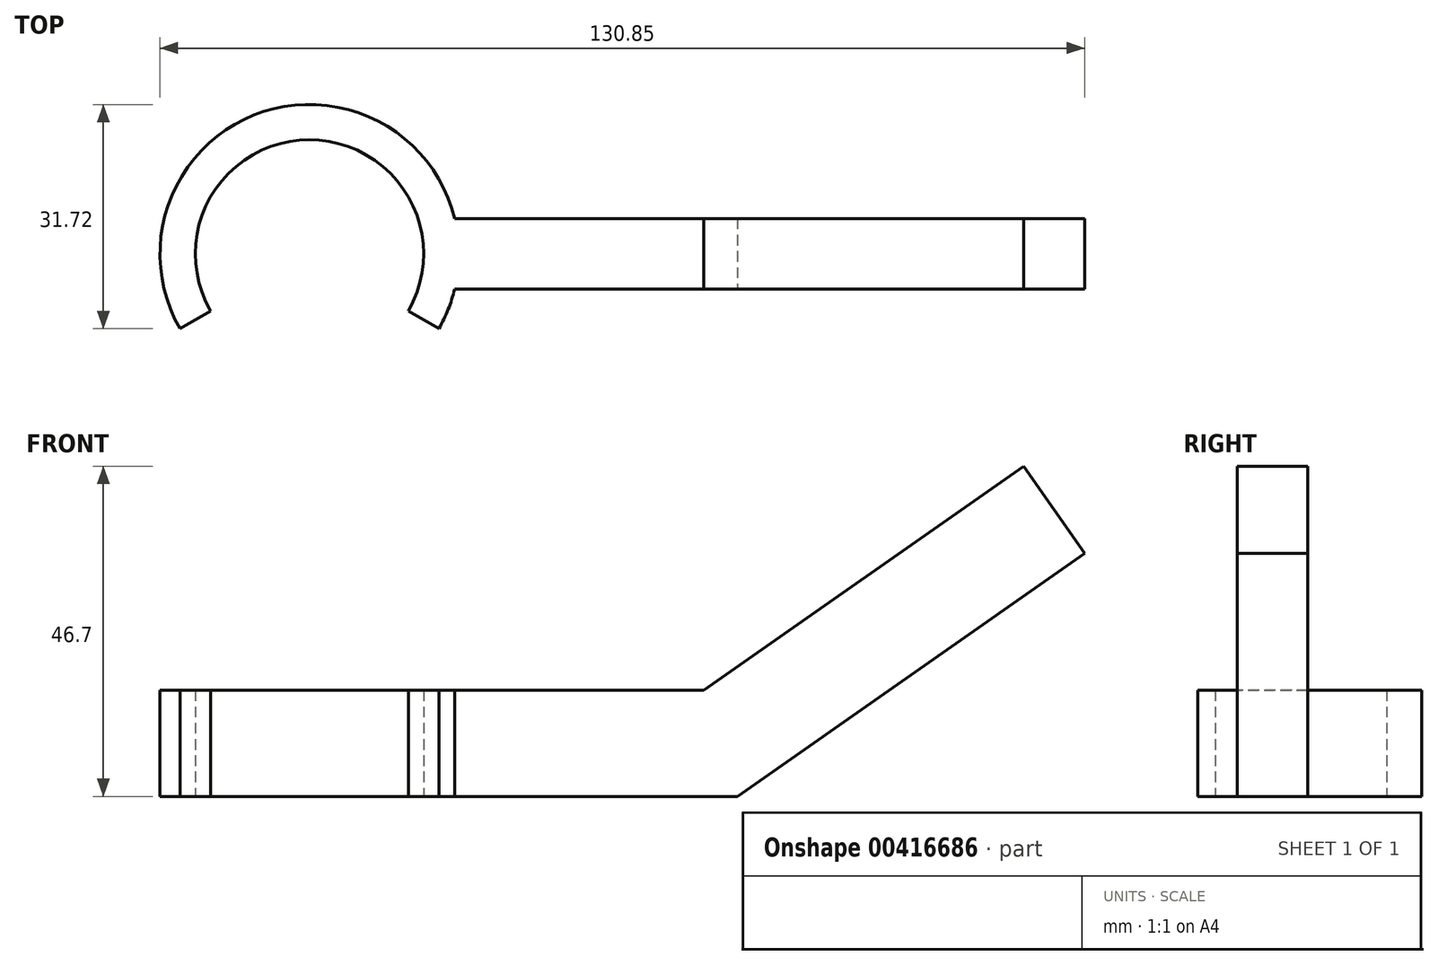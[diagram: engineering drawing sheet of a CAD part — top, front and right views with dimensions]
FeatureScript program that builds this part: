
annotation { "Feature Type Name" : "Feature", "Feature Type Description" : "" }
export const myFeature = defineFeature(function(context is Context, id is Id, definition is map)
    precondition{}
    {
        {
            var Q0;
            Q0=qCreatedBy(makeId("Top.planeOp"),FACE);
            var sketch = newSketch(context, id + "F0", { "sketchPlane" : qUnion([Q0])});
            skLineSegment(sketch, "E0", {"start": v(0, 0) * mm, "end": v(-24.9, -14.37) * mm, "construction": true});
            skLineSegment(sketch, "E1", {"start": v(0, 0) * mm, "end": v(22.76, -13.14) * mm, "construction": true});
            skPoint(sketch, "E2", {"position": v(-13.99, -8.08) * mm});
            skPoint(sketch, "E3", {"position": v(13.99, -8.07) * mm});
            skPoint(sketch, "E4", {"position": v(-18.32, -10.58) * mm});
            skPoint(sketch, "E5", {"position": v(18.32, -10.57) * mm});
            skSolve(sketch);
        }
        {
            var Q0;
            Q0=qCreatedBy(makeId("Top.planeOp"),FACE);
            var sketch = newSketch(context, id + "F1", { "sketchPlane" : qUnion([Q0])});
            skArc(sketch, "E6", {"start": v(13.99, -8.07) * mm, "mid": v(0, 16.15) * mm, "end": v(-13.99, -8.07) * mm});
            skArc(sketch, "E7", {"start": v(18.32, -10.57) * mm, "mid": v(0, 21.15) * mm, "end": v(-18.32, -10.58) * mm});
            skLineSegment(sketch, "E8", {"start": v(-13.99, -8.08) * mm, "end": v(-18.32, -10.58) * mm});
            skLineSegment(sketch, "E9", {"start": v(13.99, -8.07) * mm, "end": v(18.32, -10.57) * mm});
            skLineSegment(sketch, "E10", {"start": v(20.55, 5) * mm, "end": v(60.55, 5) * mm});
            skLineSegment(sketch, "E11", {"start": v(20.55, -5) * mm, "end": v(60.55, -5) * mm});
            skLineSegment(sketch, "E12", {"start": v(60.55, 5) * mm, "end": v(60.55, -5) * mm});
            skSolve(sketch);
        }
        {
            var Q0;
            Q0=makeQuery(id+"F1.imprint","IMPRINT",FACE,{"disambiguationData":[TD([[makeQuery(id+"F1.imprint","IMPRINT",EDGE,{"derivedFrom":sQuery(id+"F1.wireOp",EDGE,"E6")}),-1.0]])]});
            var Q1;
            {var subQ0=sQuery(id+"F1.wireOp",EDGE,"E10");Q1=makeQuery(id+"F1.imprint","IMPRINT",FACE,{"disambiguationData":[TD([[makeQuery(id+"F1.imprint","IMPRINT",EDGE,{"derivedFrom":subQ0}),-1.0]])]});}
            extrude(context, id + "F2", {"entities" : qUnion([Q0, Q1]), "depth" : 15 * mm});
        }
        {
            var Q0;
            Q0=sQuery(id+"F1.wireOp",VERTEX,"E12.start");
            var Q1;
            Q1=qCreatedBy(makeId("Front.planeOp"),FACE);
            cPlane(context, id + "F3", {"entities" : qUnion([Q0, Q1]), "cplaneType" : CPlaneType.PLANE_POINT, "offset" : 25 * mm, "width" : 150 * mm, "height" : 150 * mm});
        }
        {
            var Q0;
            Q0=sQuery(id+"F1.wireOp",VERTEX,"E11.end");
            var Q1;
            Q1=qCreatedBy(makeId("Front.planeOp"),FACE);
            cPlane(context, id + "F4", {"entities" : qUnion([Q0, Q1]), "cplaneType" : CPlaneType.PLANE_POINT, "offset" : 25 * mm, "width" : 150 * mm, "height" : 150 * mm});
        }
        {
            var Q0;
            Q0=qCreatedBy(id+"F3.planeOp",FACE);
            var sketch = newSketch(context, id + "F5", { "sketchPlane" : qUnion([Q0])});
            skLineSegment(sketch, "E13", {"start": v(60.55, 0) * mm, "end": v(109.7, 34.41) * mm});
            skSolve(sketch);
        }
        {
            var Q0;
            Q0=qCreatedBy(id+"F4.planeOp",FACE);
            var sketch = newSketch(context, id + "F6", { "sketchPlane" : qUnion([Q0])});
            skLineSegment(sketch, "E14", {"start": v(60.55, 0) * mm, "end": v(109.7, 34.41) * mm});
            skSolve(sketch);
        }
        {
            var Q0;
            Q0=sQuery(id+"F5.wireOp",VERTEX,"E13.end");
            var Q1;
            Q1=qCreatedBy(makeId("Top.planeOp"),FACE);
            cPlane(context, id + "F7", {"entities" : qUnion([Q0, Q1]), "cplaneType" : CPlaneType.PLANE_POINT, "offset" : 25 * mm, "width" : 150 * mm, "height" : 150 * mm});
        }
        {
            var Q0;
            Q0=qCreatedBy(id+"F7.planeOp",FACE);
            var sketch = newSketch(context, id + "F8", { "sketchPlane" : qUnion([Q0])});
            skLineSegment(sketch, "E15", {"start": v(109.7, 5) * mm, "end": v(109.7, -5) * mm});
            skSolve(sketch);
        }
        {
            var Q0;
            Q0=sQuery(id+"F5.wireOp",EDGE,"E13");
            cPoint(context, id + "F9", {"entities" : qUnion([Q0]), "parameter" : 0.5});
        }
        {
            var Q0;
            Q0=sQuery(id+"F5.wireOp",VERTEX,"E13.start");
            var Q1;
            Q1 = qCreatedBy(id + "F9" ,VERTEX);
            var Q2;
            Q2=sQuery(id+"F8.wireOp",VERTEX,"E15.end");
            cPlane(context, id + "F10", {"entities" : qUnion([Q0, Q1, Q2]), "cplaneType" : CPlaneType.THREE_POINT, "offset" : 25 * mm, "width" : 150 * mm, "height" : 150 * mm});
        }
        {
            var Q0;
            Q0=qCreatedBy(id+"F10.planeOp",FACE);
            var sketch = newSketch(context, id + "F11", { "sketchPlane" : qUnion([Q0])});
            skLineSegment(sketch, "E16", {"start": v(49.6, 5) * mm, "end": v(109.6, 5) * mm});
            skLineSegment(sketch, "E17", {"start": v(49.6, -5) * mm, "end": v(109.6, -5) * mm});
            skLineSegment(sketch, "E18", {"start": v(109.6, 5) * mm, "end": v(109.6, -5) * mm});
            skLineSegment(sketch, "E19", {"start": v(49.6, 5) * mm, "end": v(49.6, -5) * mm});
            skSolve(sketch);
        }
        {
            var Q0;
            Q0=makeQuery(id+"F11.imprint","IMPRINT",FACE,{"disambiguationData":[TD([[makeQuery(id+"F11.imprint","IMPRINT",EDGE,{"derivedFrom":sQuery(id+"F11.wireOp",EDGE,"E16")}),-1.0]])]});
            extrude(context, id + "F12", {"entities" : qUnion([Q0]), "operationType" : NewBodyOperationType.ADD, "depth" : 15 * mm});
        }
    });
